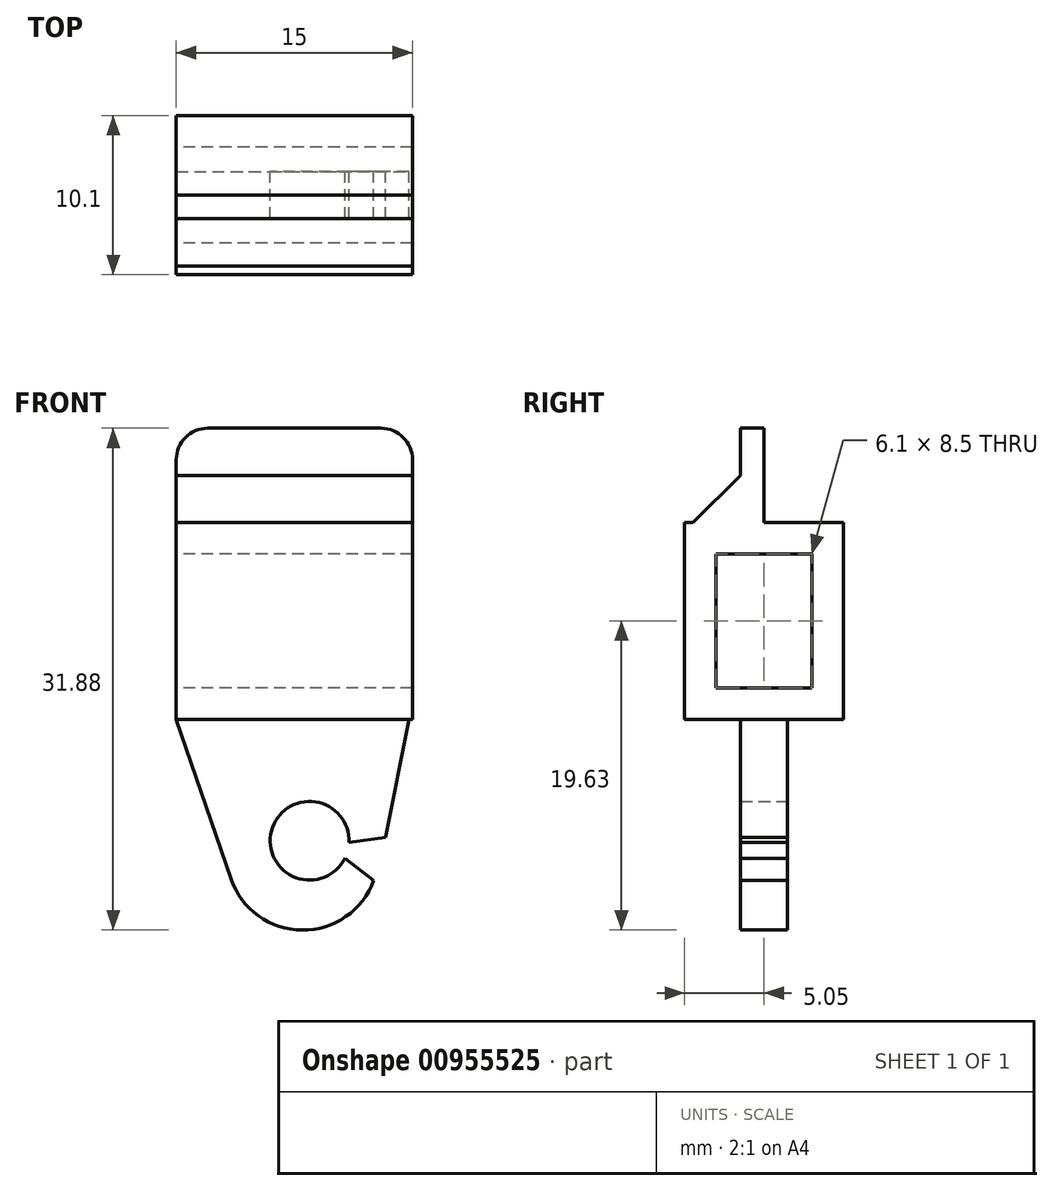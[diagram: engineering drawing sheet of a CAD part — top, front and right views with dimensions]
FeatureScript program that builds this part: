
annotation { "Feature Type Name" : "Feature", "Feature Type Description" : "" }
export const myFeature = defineFeature(function(context is Context, id is Id, definition is map)
    precondition{}
    {
        {
            var Q0;
            Q0=qCreatedBy(makeId("Right.planeOp"),FACE);
            var sketch = newSketch(context, id + "F0", { "sketchPlane" : qUnion([Q0])});
            skLineSegment(sketch, "E0.bottom", {"start": v(3.05, 4.25) * mm, "end": v(-3.05, 4.25) * mm});
            skLineSegment(sketch, "E0.top", {"start": v(3.05, -4.25) * mm, "end": v(-3.05, -4.25) * mm});
            skLineSegment(sketch, "E0.left", {"start": v(3.05, 4.25) * mm, "end": v(3.05, -4.25) * mm});
            skLineSegment(sketch, "E0.right", {"start": v(-3.05, 4.25) * mm, "end": v(-3.05, -4.25) * mm});
            skPoint(sketch, "E0.middle", {"position": v(0, 0) * mm});
            skLineSegment(sketch, "E1.bottom", {"start": v(5.05, 6.25) * mm, "end": v(-5.05, 6.25) * mm});
            skLineSegment(sketch, "E1.top", {"start": v(5.05, -6.25) * mm, "end": v(-5.05, -6.25) * mm});
            skLineSegment(sketch, "E1.left", {"start": v(5.05, 6.25) * mm, "end": v(5.05, -6.25) * mm});
            skLineSegment(sketch, "E1.right", {"start": v(-5.05, 6.25) * mm, "end": v(-5.05, -6.25) * mm});
            skSolve(sketch);
        }
        {
            var Q0;
            Q0=makeQuery(id+"F0.imprint","IMPRINT",FACE,{"disambiguationData":[TD([[makeQuery(id+"F0.imprint","IMPRINT",EDGE,{"derivedFrom":sQuery(id+"F0.wireOp",EDGE,"E0.bottom")}),-1.0]])]});
            var Q1;
            Q1=qConstructionFilter(qBodyType(qCreatedBy(id+"F0",EDGE),BodyType.WIRE),ConstructionObject.NO);
            extrude(context, id + "F1", {"entities" : qUnion([Q0]), "surfaceEntities" : qUnion([Q1]), "depth" : 15 * mm, "offsetDistance" : 25 * mm});
        }
        {
            var Q0;
            Q0=qCreatedBy(makeId("Front.planeOp"),FACE);
            var sketch = newSketch(context, id + "F2", { "sketchPlane" : qUnion([Q0])});
            skLineSegment(sketch, "E2", {"start": v(0, -6.25) * mm, "end": v(14.77, -6.25) * mm});
            skArc(sketch, "E3", {"start": v(10.96, -14.07) * mm, "mid": v(6.05, -13.34) * mm, "end": v(10.7, -15.07) * mm});
            skLineSegment(sketch, "E4", {"start": v(0, -6.25) * mm, "end": v(3.49, -16.4) * mm});
            skArc(sketch, "E5", {"start": v(3.49, -16.4) * mm, "mid": v(7.99, -19.63) * mm, "end": v(12.54, -16.47) * mm});
            skLineSegment(sketch, "E6", {"start": v(14.77, -6.25) * mm, "end": v(13.28, -13.76) * mm});
            skLineSegment(sketch, "E7", {"start": v(12.54, -16.47) * mm, "end": v(10.7, -15.07) * mm});
            skLineSegment(sketch, "E8", {"start": v(13.28, -13.76) * mm, "end": v(10.96, -14.07) * mm});
            skPoint(sketch, "E9", {"position": v(0, 0) * mm});
            skLineSegment(sketch, "E10.0", {"start": v(15, -6.25) * mm, "end": v(0, -6.25) * mm, "construction": true});
            skSolve(sketch);
        }
        {
            var Q0;
            Q0=makeQuery(id+"F2.imprint","IMPRINT",FACE,{"disambiguationData":[TD([[makeQuery(id+"F2.imprint","IMPRINT",EDGE,{"derivedFrom":sQuery(id+"F2.wireOp",EDGE,"E2")}),-1.0]])]});
            extrude(context, id + "F3", {"entities" : qUnion([Q0]), "operationType" : NewBodyOperationType.ADD, "endBound" : BoundingType.SYMMETRIC, "depth" : 3 * mm, "offsetDistance" : 25 * mm});
        }
        {
            var Q0;
            Q0=qCreatedBy(makeId("Front.planeOp"),FACE);
            var sketch = newSketch(context, id + "F4", { "sketchPlane" : qUnion([Q0])});
            skLineSegment(sketch, "E11.bottom", {"start": v(0, 6.25) * mm, "end": v(15, 6.25) * mm});
            skLineSegment(sketch, "E11.top", {"start": v(2, 12.25) * mm, "end": v(13, 12.25) * mm});
            skLineSegment(sketch, "E11.left", {"start": v(0, 6.25) * mm, "end": v(0, 10.25) * mm});
            skLineSegment(sketch, "E11.right", {"start": v(15, 6.25) * mm, "end": v(15, 10.25) * mm});
            skPoint(sketch, "E12.visualSharp", {"position": v(0, 12.25) * mm});
            skArc(sketch, "E12.filletArc", {"start": v(2, 12.25) * mm, "mid": v(0.59, 11.66) * mm, "end": v(0, 10.25) * mm});
            skPoint(sketch, "E13.visualSharp", {"position": v(15, 12.25) * mm});
            skArc(sketch, "E13.filletArc", {"start": v(15, 10.25) * mm, "mid": v(14.41, 11.66) * mm, "end": v(13, 12.25) * mm});
            skSolve(sketch);
        }
        {
            var Q0;
            Q0=qSketchRegion(id+"F4",true);
            extrude(context, id + "F5", {"entities" : qUnion([Q0]), "operationType" : NewBodyOperationType.ADD, "depth" : 1.5 * mm, "offsetDistance" : 25 * mm});
        }
        {
            var Q0;
            Q0=makeQuery(id+"F5.opExtrude","CAP_EDGE",EDGE,{"disambiguationData":[OSD([sQuery(id+"F4.wireOp",EDGE,"E11.bottom")])],"isStart":false});
            var Q1;
            Q1=makeQuery(id+"F3.opExtrude","CAP_EDGE",EDGE,{"disambiguationData":[OSD([sQuery(id+"F2.wireOp",EDGE,"E2")])],"isStart":false});
            var Q2;
            Q2=makeQuery(id+"F3.opExtrude","CAP_EDGE",EDGE,{"disambiguationData":[OSD([sQuery(id+"F2.wireOp",EDGE,"E2")])],"isStart":true});
            chamfer(context, id + "F6", {"entities" : qUnion([Q0, Q1, Q2]), "width" : 3 * mm, "tangentPropagation" : true});
        }
    });
